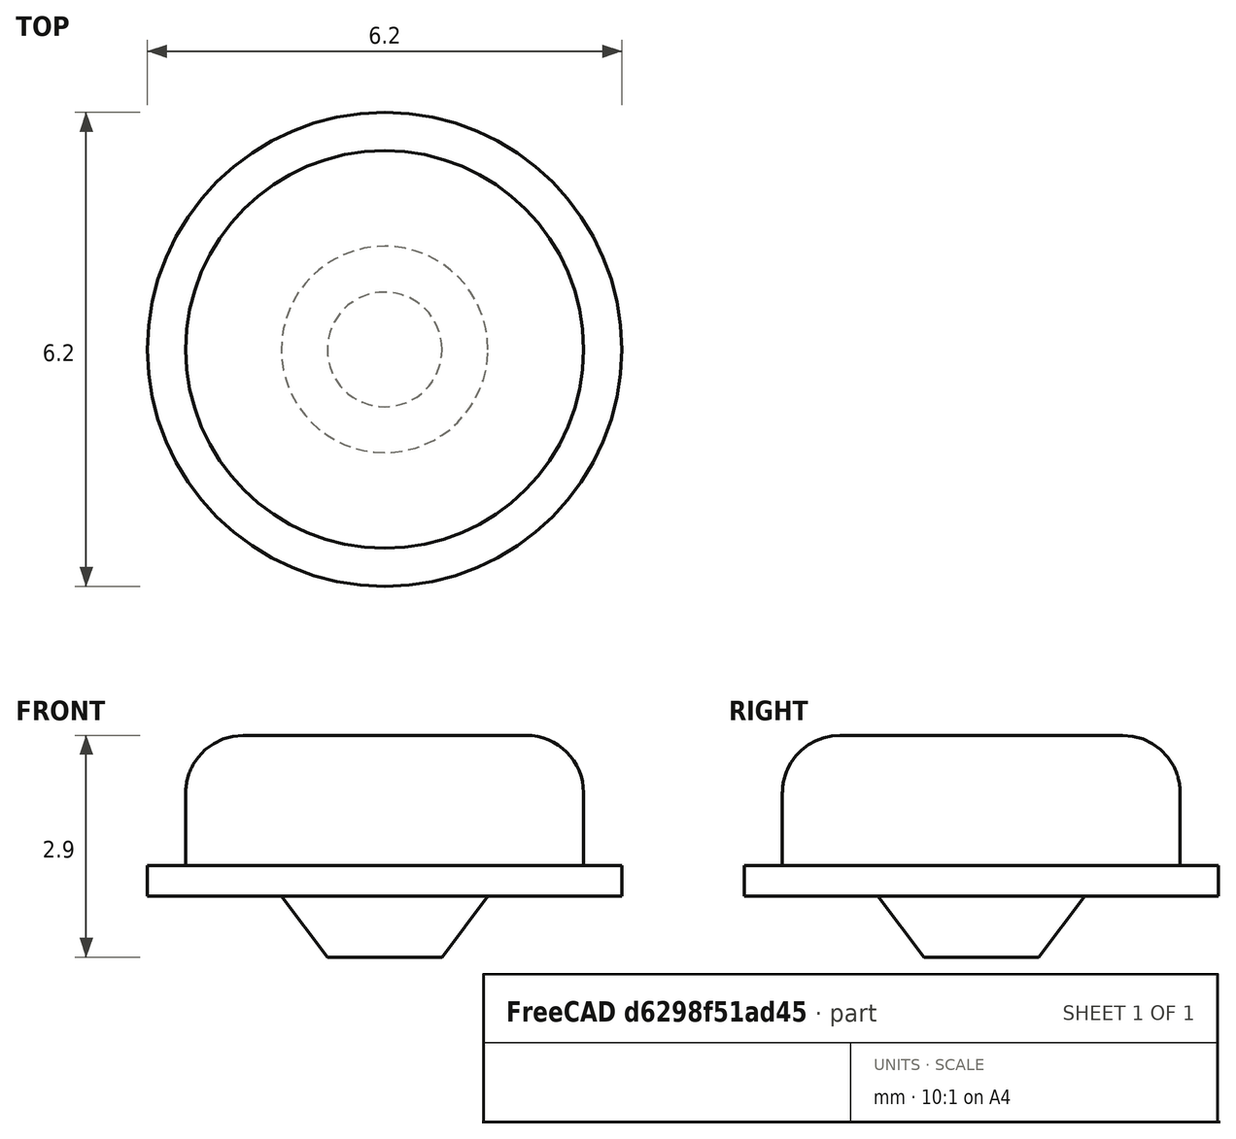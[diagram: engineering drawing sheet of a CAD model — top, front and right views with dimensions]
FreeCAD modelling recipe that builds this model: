
FCSTD DOCUMENT  (FreeCAD 0.18R0.18.4)
Label: Button
Comment: CERN Open Hardware Licence Version 2 - Weakly Reciprocal
License: Other
LicenseURL: https://ohwr.org/cern_ohl_w_v2.pdf
objects: Sketcher::SketchObject×1, PartDesign::Revolution×1, PartDesign::Body×1
note: 4 computed .brp shape members not serialized (recipe doc carries the construction recipe); baked Part::Feature solids carry a one-line shape summary decoded from their .brp

FEATURE [Sketcher::SketchObject] Sketch
  MapMode = 5
  Placement = pos=(0,0,0) rot=(1,0,0;1.5708rad)
  Support = -> [XZ_Plane]
  sketch-geometry (9):
    g0: LineSegment StartX=0 StartY=0 StartZ=0 EndX=0.75 EndY=0 EndZ=0
    g1: LineSegment StartX=3.1 StartY=0.8 StartZ=0 EndX=3.1 EndY=1.2 EndZ=0
    g2: LineSegment StartX=1.85 StartY=2.9 StartZ=0 EndX=0 EndY=2.9 EndZ=0
    g3: LineSegment StartX=0 StartY=2.9 StartZ=0 EndX=0 EndY=0 EndZ=0
    g4: LineSegment StartX=0.75 StartY=0 StartZ=0 EndX=1.35 EndY=0.8 EndZ=0
    g5: LineSegment StartX=2.6 StartY=2.15 StartZ=0 EndX=2.6 EndY=1.2 EndZ=0
    g6: LineSegment StartX=2.6 StartY=1.2 StartZ=0 EndX=3.1 EndY=1.2 EndZ=0
    g7: LineSegment StartX=1.35 StartY=0.8 StartZ=0 EndX=3.1 EndY=0.8 EndZ=0
    g8: ArcOfCircle CenterX=1.85 CenterY=2.15 CenterZ=0 NormalX=0 NormalY=0 NormalZ=1 AngleXU=0 Radius=0.75 StartAngle=0 EndAngle=1.5708
  constraints (25):
    c: Coincident(g2,g3)
    c: Coincident(g3,g0)
    c: Horizontal(g0)
    c: Horizontal(g2)
    c: Vertical(g1)
    c: Vertical(g3)
    c: Distance(g2,g0) = 2.9
    c: Vertical(g5)
    c: Horizontal(g6)
    c: Coincident(g0,g4)
    c: Distance(g0) = 0.75
    c: Horizontal(g7)
    c: Coincident(g1,g7)
    c: Coincident(g1,g6)
    c: Distance(g2,g5) = 2.6
    c: Tangent(g5,g8) = 1.5708
    c: Tangent(g2,g8) = -1.5708
    c: Radius(g8) = 0.75
    c: Coincident(g0,g-1)
    c: Coincident(g6,g5)
    c: Coincident(g7,g4)
    c: DistanceY(g0,g4) = 0.8
    c: DistanceY(g1,g1) = 0.4
    c: Distance(g1,g3) = 3.1
    c: Angle(g4,g0) = 2.2143
FEATURE [PartDesign::Revolution] Revolution
  Angle = 360
  Axis = (0,2e-16,1)
  Base = (0,0,0)
  Placement = pos=(0,0,0) rot=(1,0,0;1.5708rad)
  Profile = -> Sketch
  ReferenceAxis = -> Sketch [V_Axis]
  Reversed = true
FEATURE [PartDesign::Body] Body
  Group = -> [Sketch,Revolution]
  Origin = -> Origin
  Tip = -> Revolution
